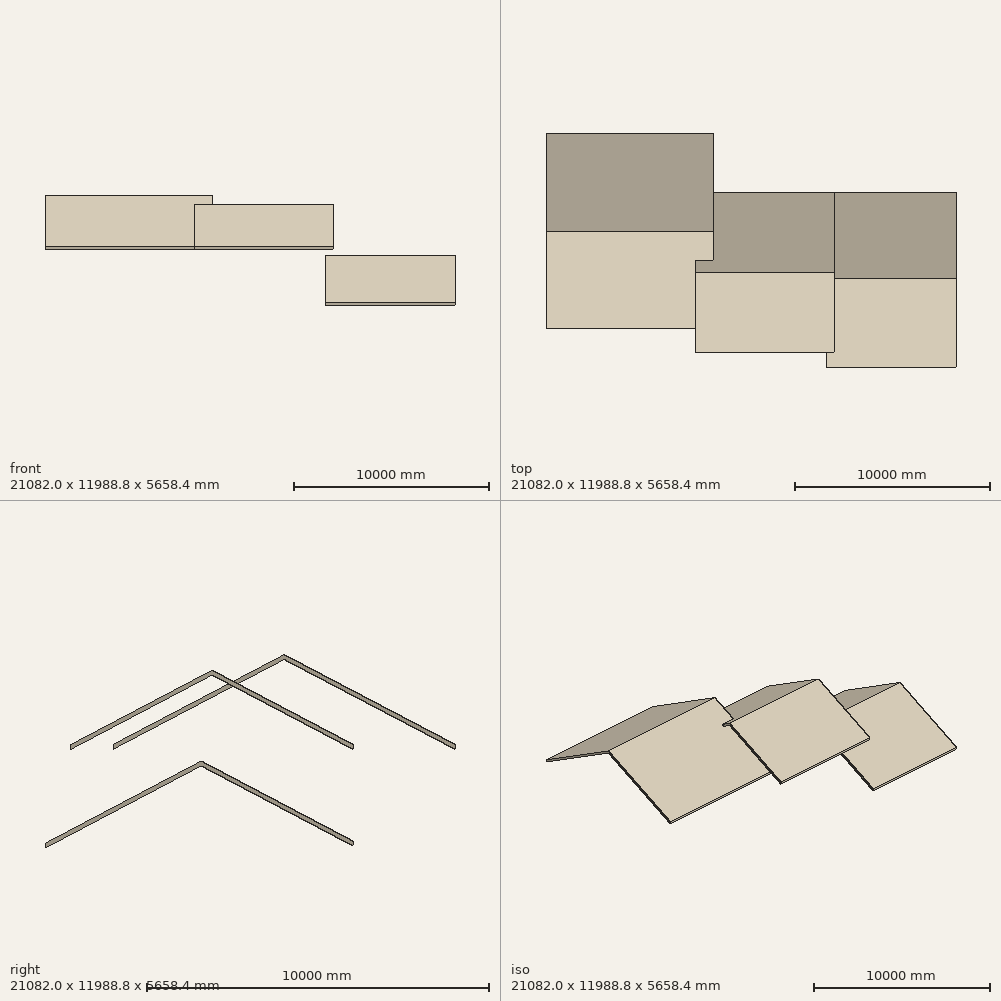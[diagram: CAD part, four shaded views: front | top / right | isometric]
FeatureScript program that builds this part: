
annotation { "Feature Type Name" : "Feature", "Feature Type Description" : "" }
export const myFeature = defineFeature(function(context is Context, id is Id, definition is map)
    precondition{}
    {
        {
            var Q0;
            Q0=qCreatedBy(makeId("Right.planeOp"),FACE);
            cPlane(context, id + "F0", {"entities" : qUnion([Q0]), "cplaneType" : CPlaneType.OFFSET, "offset" : 6248.4 * mm, "width" : 152.4 * mm, "height" : 152.4 * mm});
        }
        {
            var Q0;
            Q0=qCreatedBy(makeId("Right.planeOp"),FACE);
            cPlane(context, id + "F1", {"entities" : qUnion([Q0]), "cplaneType" : CPlaneType.OFFSET, "offset" : 7670.8 * mm, "oppositeDirection" : true, "width" : 152.4 * mm, "height" : 152.4 * mm});
        }
        {
            var Q0;
            Q0=qCreatedBy(makeId("Right.planeOp"),FACE);
            cPlane(context, id + "F2", {"entities" : qUnion([Q0]), "cplaneType" : CPlaneType.OFFSET, "offset" : 6705.6 * mm, "width" : 152.4 * mm, "height" : 152.4 * mm});
        }
        {
            var Q0;
            Q0=qCreatedBy(makeId("Right.planeOp"),FACE);
            cPlane(context, id + "F3", {"entities" : qUnion([Q0]), "cplaneType" : CPlaneType.OFFSET, "offset" : 8128 * mm, "oppositeDirection" : true, "width" : 152.4 * mm, "height" : 152.4 * mm});
        }
        {
            var Q0;
            Q0=qCreatedBy(id+"F3.planeOp",FACE);
            var sketch = newSketch(context, id + "F4", { "sketchPlane" : qUnion([Q0])});
            skLineSegment(sketch, "E0", {"start": v(10769.6, 5855.9) * mm, "end": v(5765.8, 8483.6) * mm});
            skLineSegment(sketch, "E1", {"start": v(5765.8, 8483.6) * mm, "end": v(762, 5855.9) * mm});
            skLineSegment(sketch, "E2.0", {"start": v(10769.6, 5999.35) * mm, "end": v(5765.8, 8627.05) * mm});
            skLineSegment(sketch, "E3.0", {"start": v(5765.8, 8627.05) * mm, "end": v(762, 5999.35) * mm});
            skLineSegment(sketch, "E4.0", {"start": v(10769.6, 5855.9) * mm, "end": v(10769.6, 5999.35) * mm});
            skLineSegment(sketch, "E5.0", {"start": v(762, 5855.9) * mm, "end": v(762, 5999.35) * mm});
            skSolve(sketch);
        }
        {
            var Q0;
            Q0=qCreatedBy(id+"F2.planeOp",FACE);
            var sketch = newSketch(context, id + "F5", { "sketchPlane" : qUnion([Q0])});
            skLineSegment(sketch, "E6", {"start": v(-482.6, 5848.31) * mm, "end": v(3657.6, 8027.67) * mm});
            skLineSegment(sketch, "E7", {"start": v(3657.6, 8027.67) * mm, "end": v(7772.4, 5861.69) * mm});
            skLineSegment(sketch, "E8.0", {"start": v(-482.6, 5848.31) * mm, "end": v(-482.6, 5991.84) * mm});
            skLineSegment(sketch, "E9.0", {"start": v(7772.4, 5861.69) * mm, "end": v(7772.4, 6005.2) * mm});
            skLineSegment(sketch, "E10.0", {"start": v(-482.6, 5991.84) * mm, "end": v(3657.6, 8171.2) * mm});
            skLineSegment(sketch, "E11.0", {"start": v(3657.6, 8171.2) * mm, "end": v(7772.4, 6005.2) * mm});
            skLineSegment(sketch, "E12.trimOffspring", {"start": v(7772.4, 6096) * mm, "end": v(7772.4, 6102.35) * mm});
            skSolve(sketch);
        }
        {
            var Q0;
            Q0=makeQuery(id+"F4.imprint","IMPRINT",FACE,{"disambiguationData":[TD([[makeQuery(id+"F4.imprint","IMPRINT",EDGE,{"derivedFrom":sQuery(id+"F4.wireOp",EDGE,"E0")}),-1.0]])]});
            extrude(context, id + "F6", {"entities" : qUnion([Q0]), "depth" : 8585.2 * mm});
        }
        {
            var Q0;
            Q0=makeQuery(id+"F5.imprint","IMPRINT",FACE,{"disambiguationData":[TD([[makeQuery(id+"F5.imprint","IMPRINT",EDGE,{"derivedFrom":sQuery(id+"F5.wireOp",EDGE,"E6")}),1.0]])]});
            extrude(context, id + "F7", {"entities" : qUnion([Q0]), "operationType" : NewBodyOperationType.ADD, "oppositeDirection" : true, "depth" : 7162.8 * mm});
        }
        {
            var Q0;
            Q0=qCreatedBy(id+"F0.planeOp",FACE);
            cPlane(context, id + "F8", {"entities" : qUnion([Q0]), "cplaneType" : CPlaneType.OFFSET, "offset" : 6705.6 * mm, "width" : 152.4 * mm, "height" : 152.4 * mm});
        }
        {
            var Q0;
            Q0=qCreatedBy(id+"F8.planeOp",FACE);
            var sketch = newSketch(context, id + "F9", { "sketchPlane" : qUnion([Q0])});
            skLineSegment(sketch, "E13.0", {"start": v(3340.1, 0) * mm, "end": v(3340.1, 7422.85) * mm});
            skLineSegment(sketch, "E14", {"start": v(3340.1, 5372.1) * mm, "end": v(7772.4, 3035.58) * mm});
            skLineSegment(sketch, "E15.0", {"start": v(7772.4, 3035.58) * mm, "end": v(7772.4, 3179.15) * mm});
            skLineSegment(sketch, "E16.0", {"start": v(-1219.2, 2968.64) * mm, "end": v(-1219.2, 3112.2) * mm});
            skLineSegment(sketch, "E17.0", {"start": v(3340.1, 5515.67) * mm, "end": v(7772.4, 3179.15) * mm});
            skLineSegment(sketch, "E18.trimOffspring", {"start": v(7772.4, 5372.1) * mm, "end": v(7772.4, 7422.85) * mm});
            skLineSegment(sketch, "E19.MirrorCS", {"start": v(3340.1, 5372.1) * mm, "end": v(-1219.2, 2968.64) * mm});
            skLineSegment(sketch, "E20.MirrorCS", {"start": v(3340.1, 5515.67) * mm, "end": v(-1219.2, 3112.2) * mm});
            skPoint(sketch, "E21.orphan", {"position": v(-1092.2, 3035.58) * mm});
            skPoint(sketch, "E22.orphan", {"position": v(-1092.2, 3179.15) * mm});
            skSolve(sketch);
        }
        {
            var Q0;
            Q0 = qSketchRegion(id + "F9", true);
            extrude(context, id + "F10", {"entities" : qUnion([Q0]), "oppositeDirection" : true, "depth" : 6705.6 * mm});
        }
    });
